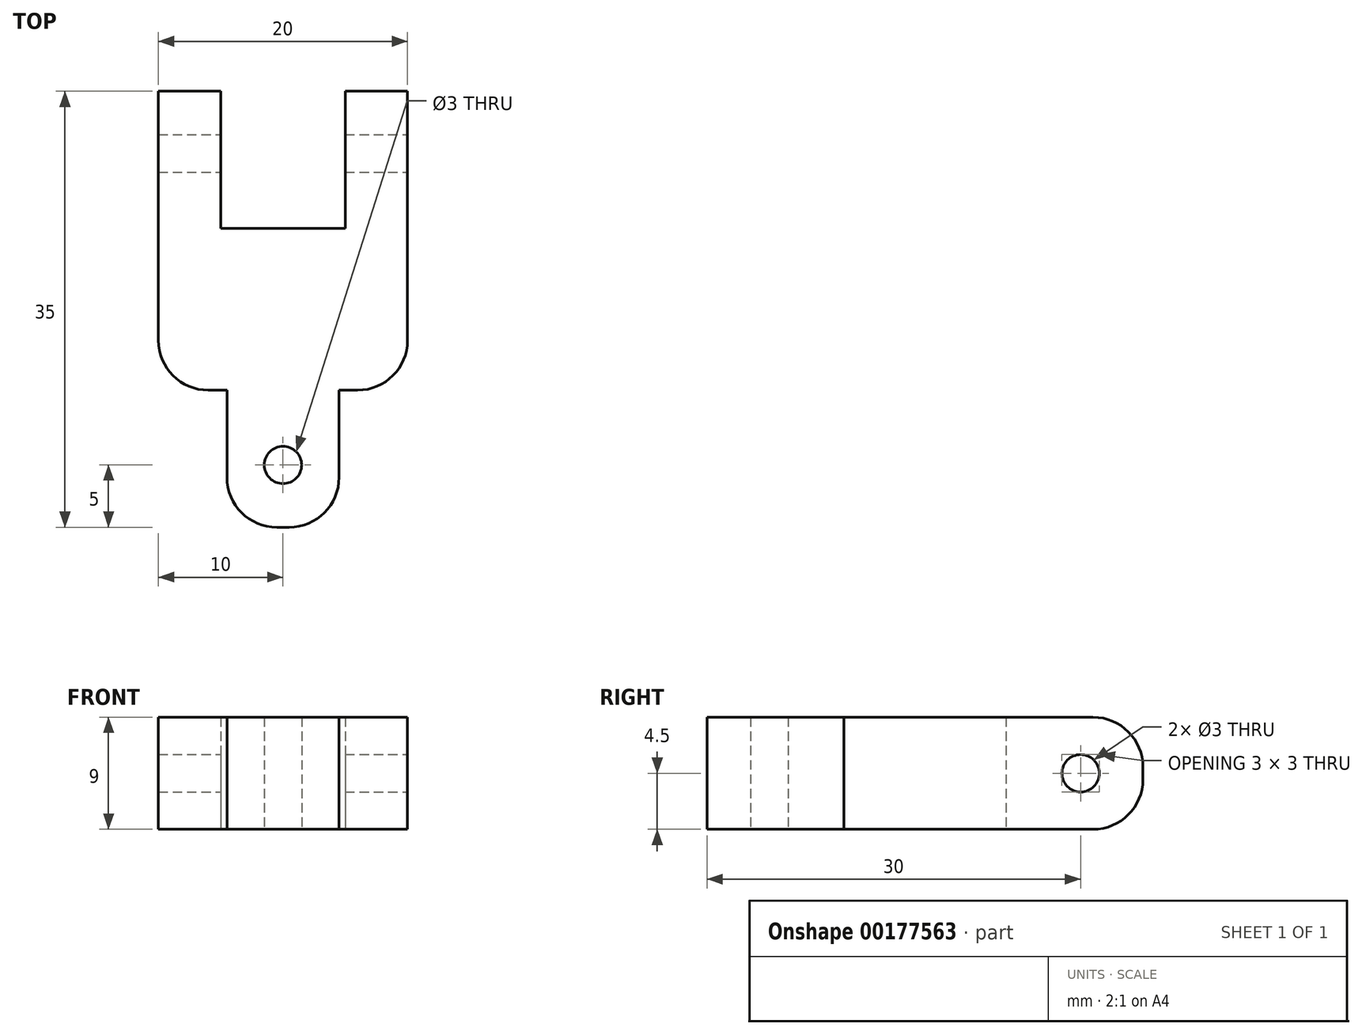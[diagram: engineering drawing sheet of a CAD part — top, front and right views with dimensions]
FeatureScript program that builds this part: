
annotation { "Feature Type Name" : "Feature", "Feature Type Description" : "" }
export const myFeature = defineFeature(function(context is Context, id is Id, definition is map)
    precondition{}
    {
        {
            var Q0;
            Q0=qCreatedBy(makeId("Top.planeOp"),FACE);
            var sketch = newSketch(context, id + "F0", { "sketchPlane" : qUnion([Q0])});
            skLineSegment(sketch, "E0.bottom", {"start": v(-10, 17.5) * mm, "end": v(-5, 17.5) * mm});
            skLineSegment(sketch, "E0.top", {"start": v(-4.5, -17.5) * mm, "end": v(4.5, -17.5) * mm});
            skLineSegment(sketch, "E0.left", {"start": v(-10, 17.5) * mm, "end": v(-10, -6.5) * mm});
            skLineSegment(sketch, "E0.right", {"start": v(10, 17.5) * mm, "end": v(10, -6.5) * mm});
            skPoint(sketch, "E0.middle", {"position": v(0, 0) * mm});
            skLineSegment(sketch, "E1.bottom", {"start": v(-10, -6.5) * mm, "end": v(-4.5, -6.5) * mm});
            skLineSegment(sketch, "E1.right", {"start": v(-4.5, -6.5) * mm, "end": v(-4.5, -17.5) * mm});
            skLineSegment(sketch, "E2.bottom", {"start": v(5, 6.5) * mm, "end": v(-5, 6.5) * mm});
            skLineSegment(sketch, "E2.left", {"start": v(5, 6.5) * mm, "end": v(5, 17.5) * mm});
            skLineSegment(sketch, "E2.right", {"start": v(-5, 6.5) * mm, "end": v(-5, 17.5) * mm});
            skPoint(sketch, "E2.middle", {"position": v(0, 17.5) * mm});
            skLineSegment(sketch, "E3.MirrorCS", {"start": v(10, -6.5) * mm, "end": v(4.5, -6.5) * mm});
            skLineSegment(sketch, "E4.MirrorCS", {"start": v(4.5, -6.5) * mm, "end": v(4.5, -17.5) * mm});
            skPoint(sketch, "E2.top.end.orphan", {"position": v(-5, 28.5) * mm});
            skPoint(sketch, "E5.orphan", {"position": v(5, 28.5) * mm});
            skLineSegment(sketch, "E6.trimOffspring", {"start": v(5, 17.5) * mm, "end": v(10, 17.5) * mm});
            skPoint(sketch, "E7.orphan", {"position": v(-10, -17.5) * mm});
            skPoint(sketch, "E8.orphan", {"position": v(10, -17.5) * mm});
            skCircle(sketch, "E9", {"center": v(0, -12.5) * mm, "radius": 1.5 * mm});
            skSolve(sketch);
        }
        {
            var Q0;
            Q0=makeQuery(id+"F0.imprint","IMPRINT",FACE,{"disambiguationData":[TD([[makeQuery(id+"F0.imprint","IMPRINT",EDGE,{"derivedFrom":sQuery(id+"F0.wireOp",EDGE,"E0.bottom")}),-1.0]])]});
            extrude(context, id + "F1", {"entities" : qUnion([Q0]), "endBound" : BoundingType.SYMMETRIC, "depth" : 9 * mm});
        }
        {
            var Q0;
            Q0=makeQuery(id+"F1.opExtrude","SWEPT_FACE",FACE,{"disambiguationData":[OSD([sQuery(id+"F0.wireOp",EDGE,"E0.right")])]});
            var sketch = newSketch(context, id + "F2", { "sketchPlane" : qUnion([Q0])});
            skCircle(sketch, "E10", {"center": v(12.5, 0) * mm, "radius": 1.5 * mm});
            skSolve(sketch);
        }
        {
            var Q0;
            Q0=makeQuery(id+"F2.imprint","IMPRINT",FACE,{"disambiguationData":[TD([[makeQuery(id+"F2.imprint","IMPRINT",EDGE,{"derivedFrom":sQuery(id+"F2.wireOp",EDGE,"E10")}),1.0]])]});
            var Q1;
            Q1=sQuery(id+"F2.wireOp",EDGE,"E10");
            extrude(context, id + "F3", {"entities" : qUnion([Q0]), "operationType" : NewBodyOperationType.REMOVE, "surfaceEntities" : qUnion([Q1]), "endBound" : BoundingType.THROUGH_ALL, "oppositeDirection" : true, "depth" : 25 * mm});
        }
        {
            var Q0;
            Q0=makeQuery(id+"F1.opExtrude","SWEPT_EDGE",EDGE,{"disambiguationData":[OSD([sQuery(id+"F0.wireOp",EDGE,"E0.top"),sQuery(id+"F0.wireOp",EDGE,"E4.MirrorCS")])]});
            var Q1;
            Q1=makeQuery(id+"F1.opExtrude","SWEPT_EDGE",EDGE,{"disambiguationData":[OSD([sQuery(id+"F0.wireOp",EDGE,"E0.top"),sQuery(id+"F0.wireOp",EDGE,"E1.right")])]});
            var Q2;
            Q2=makeQuery(id+"F1.opExtrude","CAP_EDGE",EDGE,{"disambiguationData":[OSD([sQuery(id+"F0.wireOp",EDGE,"E6.trimOffspring")])],"isStart":false});
            var Q3;
            Q3=makeQuery(id+"F1.opExtrude","CAP_EDGE",EDGE,{"disambiguationData":[OSD([sQuery(id+"F0.wireOp",EDGE,"E6.trimOffspring")])],"isStart":true});
            var Q4;
            Q4=makeQuery(id+"F1.opExtrude","CAP_EDGE",EDGE,{"disambiguationData":[OSD([sQuery(id+"F0.wireOp",EDGE,"E0.bottom")])],"isStart":true});
            var Q5;
            Q5=makeQuery(id+"F1.opExtrude","CAP_EDGE",EDGE,{"disambiguationData":[OSD([sQuery(id+"F0.wireOp",EDGE,"E0.bottom")])],"isStart":false});
            var Q6;
            Q6=makeQuery(id+"F1.opExtrude","SWEPT_EDGE",EDGE,{"disambiguationData":[OSD([sQuery(id+"F0.wireOp",EDGE,"E0.right"),sQuery(id+"F0.wireOp",EDGE,"E3.MirrorCS")])]});
            var Q7;
            Q7=makeQuery(id+"F1.opExtrude","SWEPT_EDGE",EDGE,{"disambiguationData":[OSD([sQuery(id+"F0.wireOp",EDGE,"E0.left"),sQuery(id+"F0.wireOp",EDGE,"E1.bottom")])]});
            fillet(context, id + "F4", {"entities" : qUnion([Q0, Q1, Q2, Q3, Q4, Q5, Q6, Q7]), "radius" : 4 * mm, "tangentPropagation" : true, "allowEdgeOverflow" : false});
        }
    });
